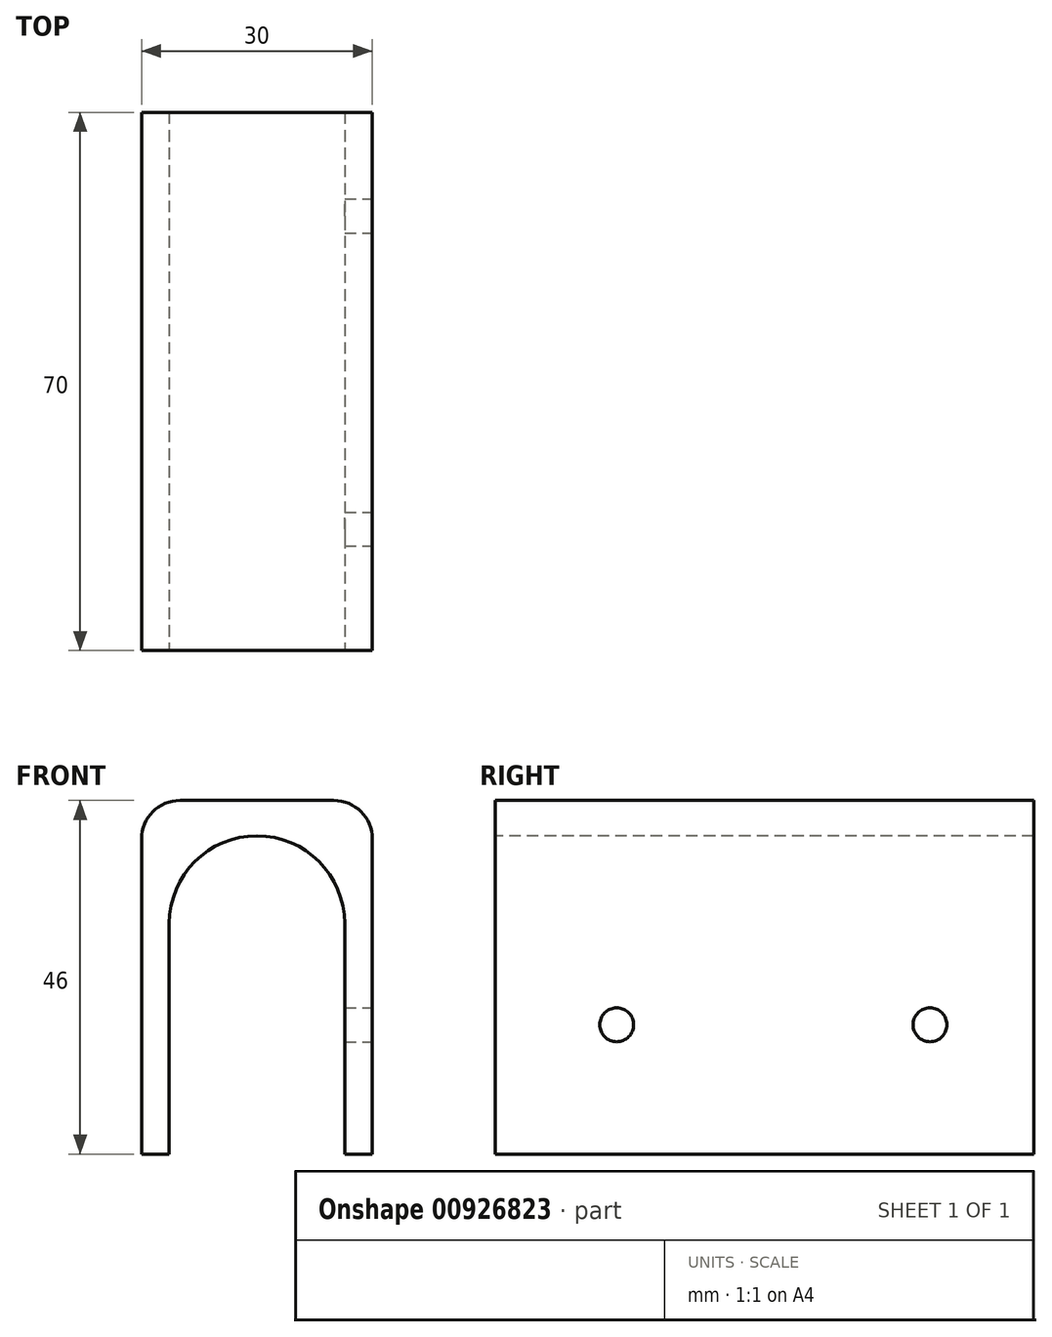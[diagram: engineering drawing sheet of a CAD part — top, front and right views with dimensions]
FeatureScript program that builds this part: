
annotation { "Feature Type Name" : "Feature", "Feature Type Description" : "" }
export const myFeature = defineFeature(function(context is Context, id is Id, definition is map)
    precondition{}
    {
        {
            var Q0;
            Q0=qCreatedBy(makeId("Front.planeOp"),FACE);
            var sketch = newSketch(context, id + "F0", { "sketchPlane" : qUnion([Q0])});
            skLineSegment(sketch, "E0.bottom", {"start": v(-7.8, 29.19) * mm, "end": v(22.2, 29.19) * mm});
            skLineSegment(sketch, "E0.top", {"start": v(-7.8, -16.81) * mm, "end": v(22.2, -16.81) * mm});
            skLineSegment(sketch, "E0.left", {"start": v(-7.8, 29.19) * mm, "end": v(-7.8, -16.81) * mm});
            skLineSegment(sketch, "E0.right", {"start": v(22.2, 29.19) * mm, "end": v(22.2, -16.81) * mm});
            skSolve(sketch);
        }
        {
            var Q0;
            Q0=makeQuery(id+"F0.imprint","IMPRINT",FACE,{"disambiguationData":[TD([[makeQuery(id+"F0.imprint","IMPRINT",EDGE,{"derivedFrom":sQuery(id+"F0.wireOp",EDGE,"E0.bottom")}),-1.0]])]});
            extrude(context, id + "F1", {"entities" : qUnion([Q0]), "depth" : 70 * mm, "offsetDistance" : 25 * mm});
        }
        {
            var Q0;
            Q0=makeQuery(id+"F1.opExtrude","CAP_FACE",FACE,{"disambiguationData":[OSD([sQuery(id+"F0.wireOp",EDGE,"E0.bottom"),sQuery(id+"F0.wireOp",EDGE,"E0.top"),sQuery(id+"F0.wireOp",EDGE,"E0.left"),sQuery(id+"F0.wireOp",EDGE,"E0.right")])],"isStart":false});
            var sketch = newSketch(context, id + "F2", { "sketchPlane" : qUnion([Q0])});
            skLineSegment(sketch, "E1.bottom", {"start": v(-4.2, 13.19) * mm, "end": v(18.6, 13.19) * mm});
            skLineSegment(sketch, "E1.top", {"start": v(-4.2, -16.81) * mm, "end": v(18.6, -16.81) * mm});
            skLineSegment(sketch, "E1.left", {"start": v(-4.2, 13.19) * mm, "end": v(-4.2, -16.81) * mm});
            skLineSegment(sketch, "E1.right", {"start": v(18.6, 13.19) * mm, "end": v(18.6, -16.81) * mm});
            skArc(sketch, "E2", {"start": v(18.6, 13.19) * mm, "mid": v(7.2, 24.59) * mm, "end": v(-4.2, 13.19) * mm});
            skSolve(sketch);
        }
        {
            var Q0;
            Q0=makeQuery(id+"F2.imprint","IMPRINT",FACE,{"disambiguationData":[TD([[makeQuery(id+"F2.imprint","IMPRINT",EDGE,{"derivedFrom":sQuery(id+"F2.wireOp",EDGE,"E1.bottom")}),1.0]])]});
            var Q1;
            Q1=makeQuery(id+"F2.imprint","IMPRINT",FACE,{"disambiguationData":[TD([[makeQuery(id+"F2.imprint","IMPRINT",EDGE,{"derivedFrom":sQuery(id+"F2.wireOp",EDGE,"E1.bottom")}),-1.0]])]});
            extrude(context, id + "F3", {"entities" : qUnion([Q0, Q1]), "operationType" : NewBodyOperationType.REMOVE, "oppositeDirection" : true, "depth" : 70 * mm, "offsetDistance" : 25 * mm});
        }
        {
            var Q0;
            Q0=makeQuery(id+"F1.opExtrude","SWEPT_FACE",FACE,{"disambiguationData":[OSD([sQuery(id+"F0.wireOp",EDGE,"E0.right")])]});
            var sketch = newSketch(context, id + "F4", { "sketchPlane" : qUnion([Q0])});
            skCircle(sketch, "E3", {"center": v(-54.21, 0) * mm, "radius": 2.2 * mm});
            skCircle(sketch, "E4", {"center": v(-13.48, 0) * mm, "radius": 2.2 * mm});
            skSolve(sketch);
        }
        {
            var Q0;
            Q0=makeQuery(id+"F4.imprint","IMPRINT",FACE,{"disambiguationData":[TD([[makeQuery(id+"F4.imprint","IMPRINT",EDGE,{"derivedFrom":sQuery(id+"F4.wireOp",EDGE,"E3")}),1.0]])]});
            var Q1;
            Q1=makeQuery(id+"F4.imprint","IMPRINT",FACE,{"disambiguationData":[TD([[makeQuery(id+"F4.imprint","IMPRINT",EDGE,{"derivedFrom":sQuery(id+"F4.wireOp",EDGE,"E4")}),1.0]])]});
            extrude(context, id + "F5", {"entities" : qUnion([Q0, Q1]), "operationType" : NewBodyOperationType.REMOVE, "endBound" : BoundingType.UP_TO_NEXT, "oppositeDirection" : true, "depth" : 100 * mm, "offsetDistance" : 25 * mm});
        }
        {
            var Q0;
            Q0=makeQuery(id+"F1.opExtrude","SWEPT_EDGE",EDGE,{"disambiguationData":[OSD([sQuery(id+"F0.wireOp",EDGE,"E0.bottom"),sQuery(id+"F0.wireOp",EDGE,"E0.left")])]});
            var Q1;
            Q1=makeQuery(id+"F1.opExtrude","SWEPT_EDGE",EDGE,{"disambiguationData":[OSD([sQuery(id+"F0.wireOp",EDGE,"E0.bottom"),sQuery(id+"F0.wireOp",EDGE,"E0.right")])]});
            fillet(context, id + "F6", {"entities" : qUnion([Q0, Q1]), "radius" : 5 * mm, "tangentPropagation" : true, "allowEdgeOverflow" : false});
        }
    });
